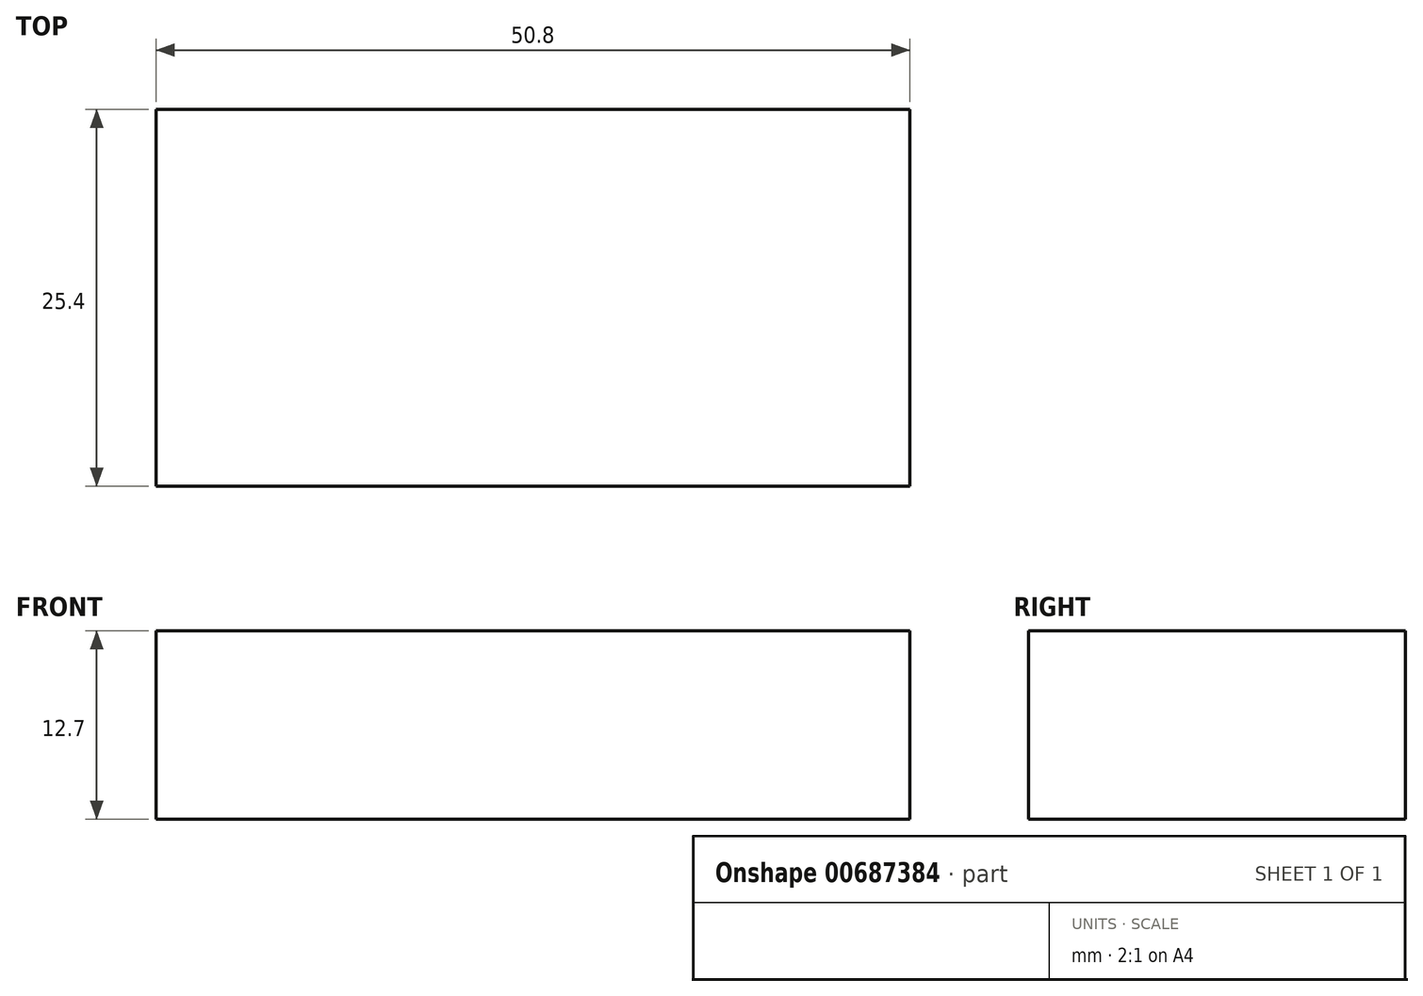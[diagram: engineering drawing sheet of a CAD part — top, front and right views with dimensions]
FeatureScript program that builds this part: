
annotation { "Feature Type Name" : "Feature", "Feature Type Description" : "" }
export const myFeature = defineFeature(function(context is Context, id is Id, definition is map)
    precondition{}
    {
        {
            var Q0;
            Q0=qCreatedBy(makeId("Top.planeOp"),FACE);
            var sketch = newSketch(context, id + "F0", { "sketchPlane" : qUnion([Q0])});
            skLineSegment(sketch, "E0.bottom", {"start": v(25.4, 12.7) * mm, "end": v(-25.4, 12.7) * mm});
            skLineSegment(sketch, "E0.top", {"start": v(25.4, -12.7) * mm, "end": v(-25.4, -12.7) * mm});
            skLineSegment(sketch, "E0.left", {"start": v(25.4, 12.7) * mm, "end": v(25.4, -12.7) * mm});
            skLineSegment(sketch, "E0.right", {"start": v(-25.4, 12.7) * mm, "end": v(-25.4, -12.7) * mm});
            skPoint(sketch, "E0.middle", {"position": v(0, 0) * mm});
            skSolve(sketch);
        }
        {
            var Q0;
            Q0 = qSketchRegion(id + "F0", true);
            extrude(context, id + "F1", {"entities" : qUnion([Q0]), "depth" : 12.7 * mm, "offsetDistance" : 25.4 * mm});
        }
    });
